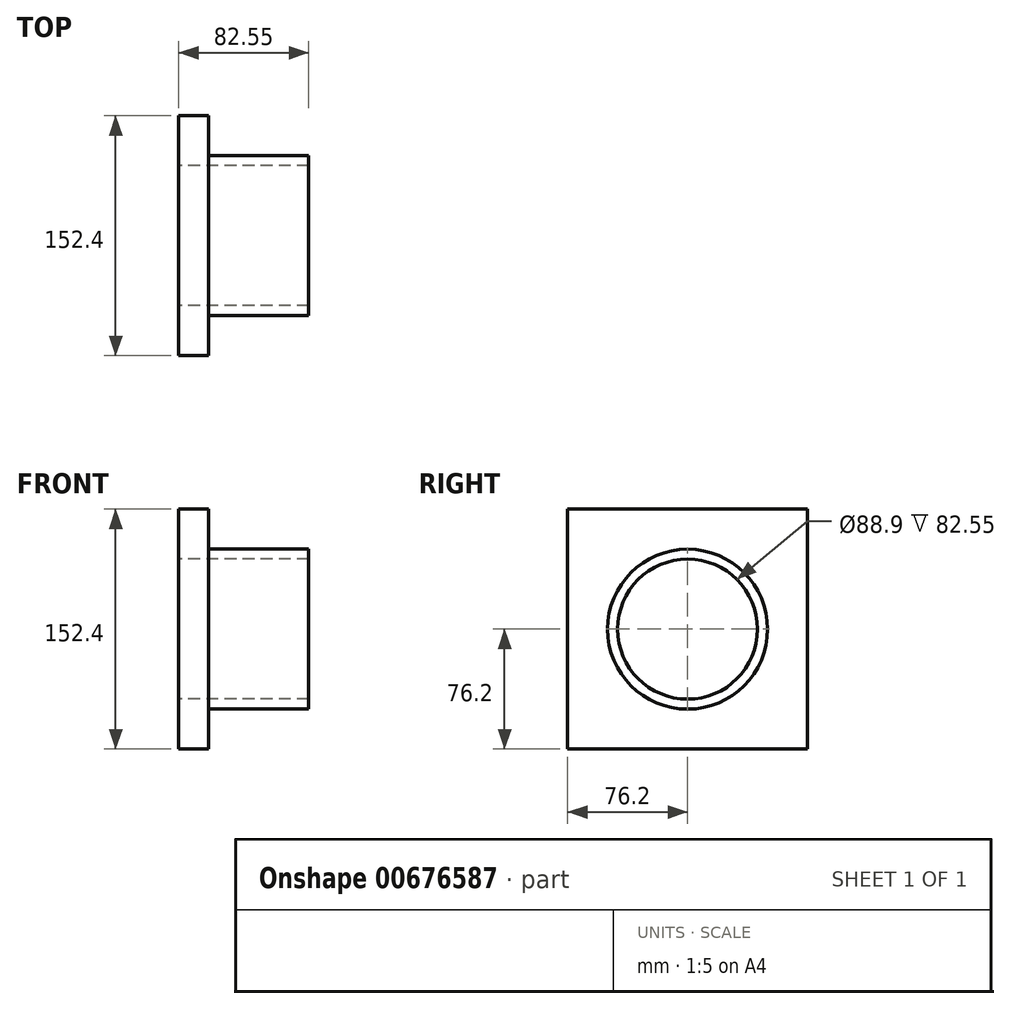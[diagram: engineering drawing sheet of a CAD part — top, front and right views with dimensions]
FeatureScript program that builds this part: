
annotation { "Feature Type Name" : "Feature", "Feature Type Description" : "" }
export const myFeature = defineFeature(function(context is Context, id is Id, definition is map)
    precondition{}
    {
        {
            var Q0;
            Q0=qCreatedBy(makeId("Right.planeOp"),FACE);
            var sketch = newSketch(context, id + "F0", { "sketchPlane" : qUnion([Q0])});
            skLineSegment(sketch, "E0.bottom", {"start": v(76.2, -76.2) * mm, "end": v(-76.2, -76.2) * mm});
            skLineSegment(sketch, "E0.top", {"start": v(76.2, 76.2) * mm, "end": v(-76.2, 76.2) * mm});
            skLineSegment(sketch, "E0.left", {"start": v(76.2, -76.2) * mm, "end": v(76.2, 76.2) * mm});
            skLineSegment(sketch, "E0.right", {"start": v(-76.2, -76.2) * mm, "end": v(-76.2, 76.2) * mm});
            skPoint(sketch, "E0.middle", {"position": v(0, 0) * mm});
            skSolve(sketch);
        }
        {
            var Q0;
            Q0 = qSketchRegion(id + "F0", true);
            extrude(context, id + "F1", {"entities" : qUnion([Q0]), "depth" : 19.05 * mm, "offsetDistance" : 25.4 * mm});
        }
        {
            var Q0;
            Q0=makeQuery(id+"F1.opExtrude","CAP_FACE",FACE,{"disambiguationData":[OSD([sQuery(id+"F0.wireOp",EDGE,"E0.bottom"),sQuery(id+"F0.wireOp",EDGE,"E0.top"),sQuery(id+"F0.wireOp",EDGE,"E0.left"),sQuery(id+"F0.wireOp",EDGE,"E0.right")])],"isStart":true});
            var sketch = newSketch(context, id + "F2", { "sketchPlane" : qUnion([Q0])});
            skCircle(sketch, "E1", {"center": v(0, 0) * mm, "radius": 44.45 * mm});
            skSolve(sketch);
        }
        {
            var Q0;
            Q0 = qSketchRegion(id + "F2", true);
            extrude(context, id + "F3", {"entities" : qUnion([Q0]), "operationType" : NewBodyOperationType.REMOVE, "endBound" : BoundingType.THROUGH_ALL, "oppositeDirection" : true, "depth" : 25.4 * mm, "offsetDistance" : 25.4 * mm});
        }
        {
            var Q0;
            Q0=makeQuery(id+"F1.opExtrude","CAP_FACE",FACE,{"disambiguationData":[OSD([sQuery(id+"F0.wireOp",EDGE,"E0.bottom"),sQuery(id+"F0.wireOp",EDGE,"E0.top"),sQuery(id+"F0.wireOp",EDGE,"E0.left"),sQuery(id+"F0.wireOp",EDGE,"E0.right")])],"isStart":false});
            var sketch = newSketch(context, id + "F4", { "sketchPlane" : qUnion([Q0])});
            skCircle(sketch, "E2", {"center": v(0, 0) * mm, "radius": 50.8 * mm});
            skSolve(sketch);
        }
        {
            var Q0;
            Q0=makeQuery(id+"F4.imprint","IMPRINT",FACE,{"disambiguationData":[TD([[makeQuery(id+"F4.imprint","IMPRINT",EDGE,{"derivedFrom":sQuery(id+"F4.wireOp",EDGE,"E2")}),1.0]])]});
            extrude(context, id + "F5", {"entities" : qUnion([Q0]), "operationType" : NewBodyOperationType.ADD, "depth" : 63.5 * mm, "offsetDistance" : 25.4 * mm});
        }
    });
